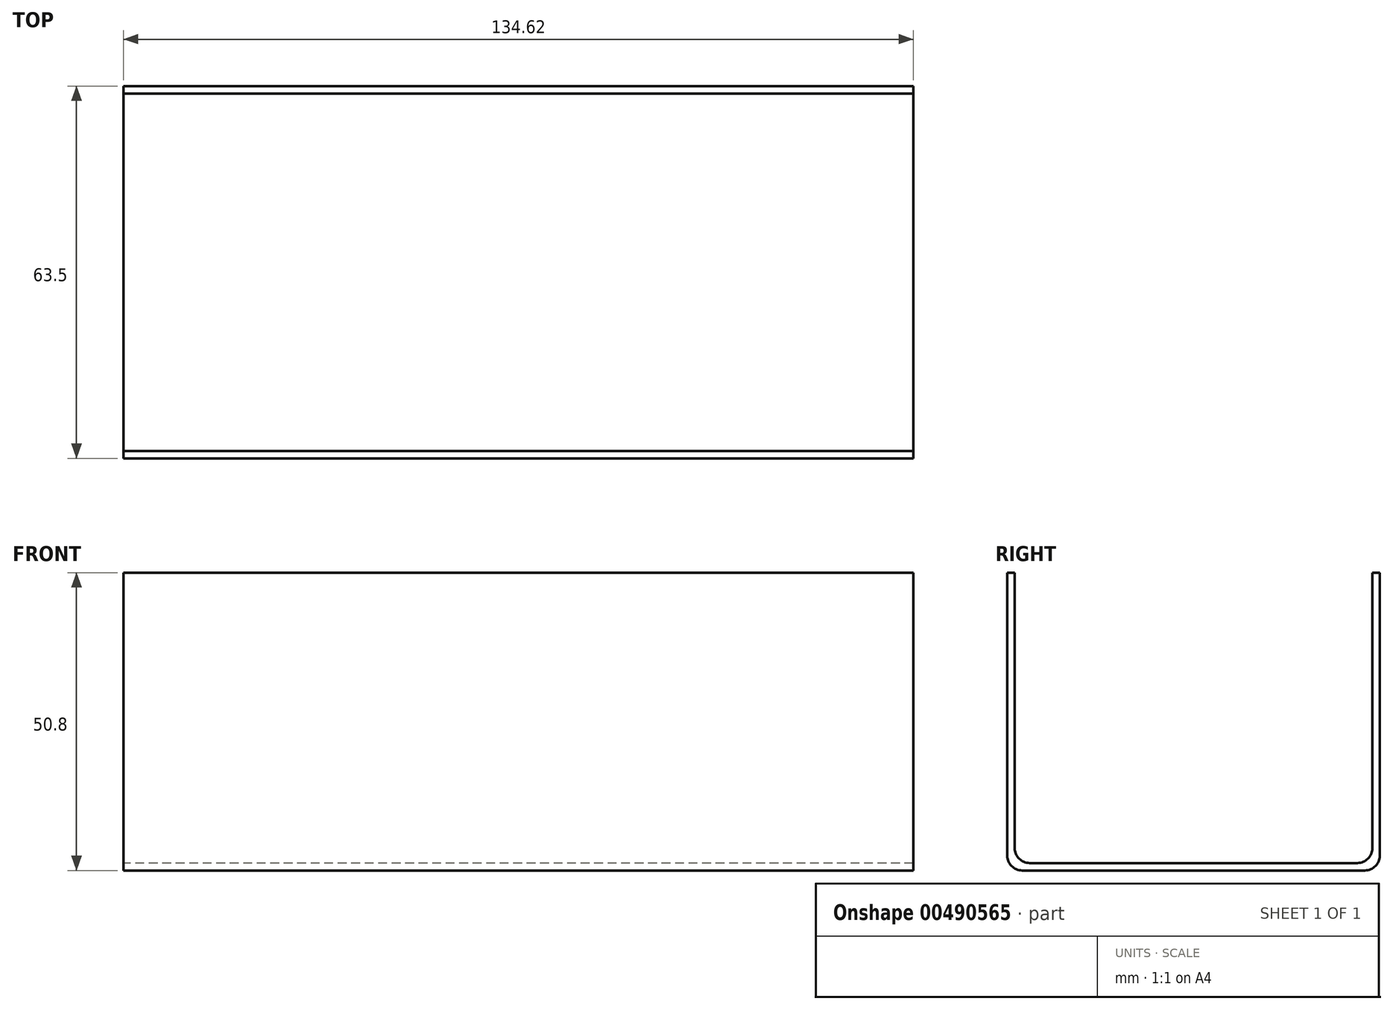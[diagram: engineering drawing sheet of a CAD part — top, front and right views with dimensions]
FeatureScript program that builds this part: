
annotation { "Feature Type Name" : "Feature", "Feature Type Description" : "" }
export const myFeature = defineFeature(function(context is Context, id is Id, definition is map)
    precondition{}
    {
        {
            var Q0;
            Q0=qCreatedBy(makeId("Top.planeOp"),FACE);
            var sketch = newSketch(context, id + "F0", { "sketchPlane" : qUnion([Q0])});
            skLineSegment(sketch, "E0.bottom", {"start": v(67.31, 31.75) * mm, "end": v(-67.31, 31.75) * mm});
            skLineSegment(sketch, "E0.top", {"start": v(67.31, -31.75) * mm, "end": v(-67.31, -31.75) * mm});
            skLineSegment(sketch, "E0.left", {"start": v(67.31, 31.75) * mm, "end": v(67.31, -31.75) * mm});
            skLineSegment(sketch, "E0.right", {"start": v(-67.31, 31.75) * mm, "end": v(-67.31, -31.75) * mm});
            skPoint(sketch, "E0.middle", {"position": v(0, 0) * mm});
            skSolve(sketch);
        }
        {
            var Q0;
            Q0=makeQuery(id+"F0.imprint","IMPRINT",FACE,{"disambiguationData":[TD([[makeQuery(id+"F0.imprint","IMPRINT",EDGE,{"derivedFrom":sQuery(id+"F0.wireOp",EDGE,"E0.bottom")}),1.0]])]});
            extrude(context, id + "F1", {"entities" : qUnion([Q0]), "depth" : 50.8 * mm});
        }
        {
            var Q0;
            Q0=makeQuery(id+"F1.opExtrude","CAP_FACE",FACE,{"disambiguationData":[OSD([sQuery(id+"F0.wireOp",EDGE,"E0.bottom"),sQuery(id+"F0.wireOp",EDGE,"E0.top"),sQuery(id+"F0.wireOp",EDGE,"E0.left"),sQuery(id+"F0.wireOp",EDGE,"E0.right")])],"isStart":false});
            var sketch = newSketch(context, id + "F2", { "sketchPlane" : qUnion([Q0])});
            skLineSegment(sketch, "E1.bottom", {"start": v(67.31, 30.48) * mm, "end": v(-67.31, 30.48) * mm});
            skLineSegment(sketch, "E1.top", {"start": v(67.31, -30.48) * mm, "end": v(-67.31, -30.48) * mm});
            skLineSegment(sketch, "E1.left", {"start": v(67.31, 30.48) * mm, "end": v(67.31, -30.48) * mm});
            skLineSegment(sketch, "E1.right", {"start": v(-67.31, 30.48) * mm, "end": v(-67.31, -30.48) * mm});
            skPoint(sketch, "E1.middle", {"position": v(0, 0) * mm});
            skSolve(sketch);
        }
        {
            var Q0;
            Q0=makeQuery(id+"F2.imprint","IMPRINT",FACE,{"disambiguationData":[TD([[makeQuery(id+"F2.imprint","IMPRINT",EDGE,{"derivedFrom":sQuery(id+"F2.wireOp",EDGE,"E1.bottom")}),1.0]])]});
            extrude(context, id + "F3", {"entities" : qUnion([Q0]), "operationType" : NewBodyOperationType.REMOVE, "oppositeDirection" : true, "depth" : 49.53 * mm});
        }
        {
            var Q0;
            Q0=makeQuery(id+"F3.boolean.opBoolean","COPY",EDGE,{"derivedFrom":makeQuery(id+"F3.opExtrude","CAP_EDGE",EDGE,{"disambiguationData":[OSD([sQuery(id+"F2.wireOp",EDGE,"E1.bottom")])],"isStart":false})});
            var Q1;
            Q1=makeQuery(id+"F3.boolean.opBoolean","COPY",EDGE,{"derivedFrom":makeQuery(id+"F3.opExtrude","CAP_EDGE",EDGE,{"disambiguationData":[OSD([sQuery(id+"F2.wireOp",EDGE,"E1.top")])],"isStart":false})});
            var Q2;
            Q2=makeQuery(id+"F1.opExtrude","CAP_EDGE",EDGE,{"disambiguationData":[OSD([sQuery(id+"F0.wireOp",EDGE,"E0.bottom")])],"isStart":true});
            var Q3;
            Q3=makeQuery(id+"F1.opExtrude","CAP_EDGE",EDGE,{"disambiguationData":[OSD([sQuery(id+"F0.wireOp",EDGE,"E0.top")])],"isStart":true});
            fillet(context, id + "F4", {"entities" : qUnion([Q0, Q1, Q2, Q3]), "radius" : 2.54 * mm, "tangentPropagation" : true, "allowEdgeOverflow" : false});
        }
    });
